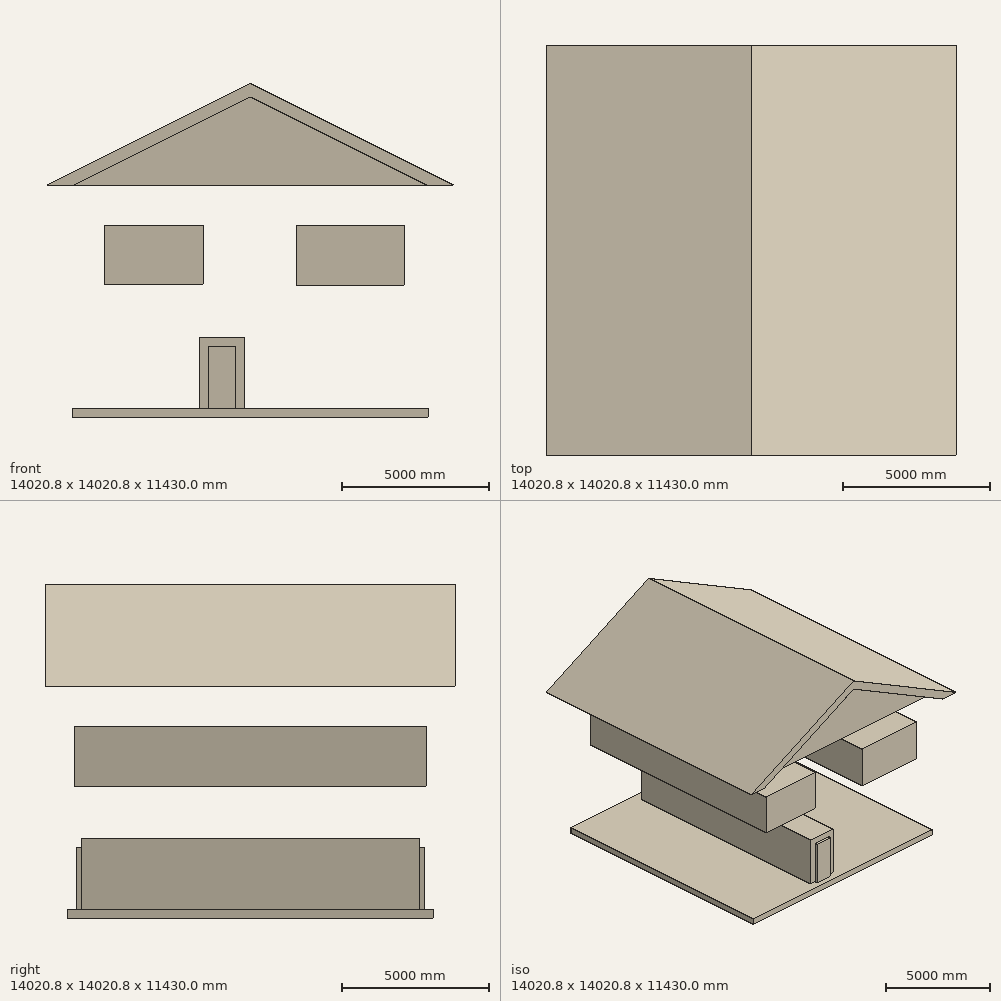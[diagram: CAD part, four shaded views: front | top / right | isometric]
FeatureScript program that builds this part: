
annotation { "Feature Type Name" : "Feature", "Feature Type Description" : "" }
export const myFeature = defineFeature(function(context is Context, id is Id, definition is map)
    precondition{}
    {
        {
            var Q0;
            Q0=qCreatedBy(makeId("Front.planeOp"),FACE);
            var sketch = newSketch(context, id + "F0", { "sketchPlane" : qUnion([Q0])});
            skLineSegment(sketch, "E0", {"start": v(0, 0) * mm, "end": v(-6096, 0) * mm});
            skLineSegment(sketch, "E1", {"start": v(0, 0) * mm, "end": v(6096, 0) * mm});
            skLineSegment(sketch, "E2", {"start": v(0, 0) * mm, "end": v(0, 3048) * mm, "construction": true});
            skLineSegment(sketch, "E3", {"start": v(-6096, 0) * mm, "end": v(0, 3048) * mm});
            skLineSegment(sketch, "E4", {"start": v(0, 3048) * mm, "end": v(6096, 0) * mm});
            skLineSegment(sketch, "E5", {"start": v(0, 3048) * mm, "end": v(0, 3505.2) * mm});
            skLineSegment(sketch, "E6", {"start": v(6096, 0) * mm, "end": v(7010.4, 0) * mm});
            skLineSegment(sketch, "E7", {"start": v(-6096, 0) * mm, "end": v(-7010.4, 0) * mm});
            skLineSegment(sketch, "E8", {"start": v(-7010.4, 0) * mm, "end": v(0, 3505.2) * mm});
            skLineSegment(sketch, "E9", {"start": v(7010.4, 0) * mm, "end": v(0, 3505.2) * mm});
            skLineSegment(sketch, "E10", {"start": v(-6096, 0) * mm, "end": v(-6096, -7620) * mm});
            skLineSegment(sketch, "E11", {"start": v(-6096, -7620) * mm, "end": v(6096, -7620) * mm});
            skLineSegment(sketch, "E12", {"start": v(6096, 0) * mm, "end": v(6096, -7315.2) * mm});
            skLineSegment(sketch, "E13", {"start": v(-6096, -7620) * mm, "end": v(-6096, -7924.8) * mm});
            skLineSegment(sketch, "E14", {"start": v(-6096, -7924.8) * mm, "end": v(6103.47, -7924.8) * mm});
            skLineSegment(sketch, "E15", {"start": v(6103.47, -7924.8) * mm, "end": v(6096, -7620) * mm});
            skLineSegment(sketch, "E16", {"start": v(-1432.56, -7620) * mm, "end": v(-1432.56, -5486.4) * mm});
            skLineSegment(sketch, "E17", {"start": v(-1432.56, -5486.4) * mm, "end": v(-518.16, -5486.4) * mm});
            skLineSegment(sketch, "E18", {"start": v(-518.16, -5486.4) * mm, "end": v(-518.16, -7620) * mm});
            skLineSegment(sketch, "E19.bottom", {"start": v(1560.33, -1350.55) * mm, "end": v(5281.06, -1350.55) * mm});
            skLineSegment(sketch, "E19.top", {"start": v(1560.33, -3402.59) * mm, "end": v(5281.06, -3402.59) * mm});
            skLineSegment(sketch, "E19.left", {"start": v(1560.33, -1350.55) * mm, "end": v(1560.33, -3402.59) * mm});
            skLineSegment(sketch, "E19.right", {"start": v(5281.06, -1350.55) * mm, "end": v(5281.06, -3402.59) * mm});
            skLineSegment(sketch, "E20.bottom", {"start": v(-5001.7, -1350.55) * mm, "end": v(-1619.33, -1350.55) * mm});
            skLineSegment(sketch, "E20.top", {"start": v(-5001.7, -3357.49) * mm, "end": v(-1619.33, -3357.49) * mm});
            skLineSegment(sketch, "E20.left", {"start": v(-5001.7, -1350.55) * mm, "end": v(-5001.7, -3357.49) * mm});
            skLineSegment(sketch, "E20.right", {"start": v(-1619.33, -1350.55) * mm, "end": v(-1619.33, -3357.49) * mm});
            skLineSegment(sketch, "E21.bottom", {"start": v(-941.03, 2243.3) * mm, "end": v(887.77, 2243.3) * mm});
            skLineSegment(sketch, "E21.top", {"start": v(-941.03, 719.3) * mm, "end": v(887.77, 719.3) * mm});
            skLineSegment(sketch, "E21.left", {"start": v(-941.03, 2243.3) * mm, "end": v(-941.03, 719.3) * mm});
            skLineSegment(sketch, "E21.right", {"start": v(887.77, 2243.3) * mm, "end": v(887.77, 719.3) * mm});
            skLineSegment(sketch, "E22.0", {"start": v(-213.36, -5181.6) * mm, "end": v(-213.36, -7620) * mm});
            skLineSegment(sketch, "E22.1", {"start": v(-1737.36, -5181.6) * mm, "end": v(-213.36, -5181.6) * mm});
            skLineSegment(sketch, "E22.2", {"start": v(-1737.36, -7620) * mm, "end": v(-1737.36, -5181.6) * mm});
            skSolve(sketch);
        }
        {
            var Q0;
            Q0=makeQuery(id+"F0.imprint","IMPRINT",FACE,{"disambiguationData":[TD([[makeQuery(id+"F0.imprint","IMPRINT",EDGE,{"derivedFrom":sQuery(id+"F0.wireOp",EDGE,"E3")}),1.0]])]});
            var Q1;
            Q1=makeQuery(id+"F0.imprint","IMPRINT",FACE,{"disambiguationData":[TD([[makeQuery(id+"F0.imprint","IMPRINT",EDGE,{"derivedFrom":sQuery(id+"F0.wireOp",EDGE,"E4")}),1.0]])]});
            extrude(context, id + "F1", {"entities" : qUnion([Q0, Q1]), "endBound" : BoundingType.SYMMETRIC, "depth" : 14020.8 * mm, "offsetDistance" : 30.48 * mm});
        }
        {
            var Q0;
            Q0=makeQuery(id+"F0.imprint","IMPRINT",FACE,{"disambiguationData":[TD([[makeQuery(id+"F0.imprint","IMPRINT",EDGE,{"derivedFrom":sQuery(id+"F0.wireOp",EDGE,"E0")}),-1.0]])]});
            extrude(context, id + "F2", {"entities" : qUnion([Q0]), "operationType" : NewBodyOperationType.ADD, "endBound" : BoundingType.SYMMETRIC, "depth" : 12496.8 * mm, "offsetDistance" : 30.48 * mm});
        }
        {
            var Q0;
            Q0=makeQuery(id+"F0.imprint","IMPRINT",FACE,{"disambiguationData":[TD([[makeQuery(id+"F0.imprint","IMPRINT",EDGE,{"derivedFrom":sQuery(id+"F0.wireOp",EDGE,"E21.bottom")}),-1.0]])]});
            extrude(context, id + "F3", {"entities" : qUnion([Q0]), "operationType" : NewBodyOperationType.ADD, "endBound" : BoundingType.SYMMETRIC, "depth" : 12496.8 * mm, "offsetDistance" : 30.48 * mm});
        }
        {
            var Q0;
            {var subQ5=sQuery(id+"F0.wireOp",EDGE,"E13");Q0=makeQuery(id+"F0.imprint","IMPRINT",FACE,{"disambiguationData":[TD([[makeQuery(id+"F0.imprint","IMPRINT",EDGE,{"derivedFrom":subQ5}),1.0]])]});}
            extrude(context, id + "F4", {"entities" : qUnion([Q0]), "endBound" : BoundingType.SYMMETRIC, "depth" : 12496.8 * mm, "offsetDistance" : 30.48 * mm});
        }
        {
            var Q0;
            Q0=sQuery(id+"F0.wireOp",EDGE,"E10");
            var Q1;
            Q1=sQuery(id+"F0.wireOp",EDGE,"E12");
            extrude(context, id + "F5", {"bodyType" : ToolBodyType.SURFACE, "surfaceEntities" : qUnion([Q0, Q1]), "endBound" : BoundingType.SYMMETRIC, "depth" : 12496.8 * mm, "offsetDistance" : 30.48 * mm});
        }
        {
            var Q0;
            Q0=makeQuery(id+"F0.imprint","IMPRINT",FACE,{"disambiguationData":[TD([[makeQuery(id+"F0.imprint","IMPRINT",EDGE,{"derivedFrom":sQuery(id+"F0.wireOp",EDGE,"E20.bottom")}),-1.0]])]});
            extrude(context, id + "F6", {"entities" : qUnion([Q0]), "endBound" : BoundingType.SYMMETRIC, "depth" : 12039.6 * mm, "offsetDistance" : 30.48 * mm});
        }
        {
            var Q0;
            Q0=makeQuery(id+"F0.imprint","IMPRINT",FACE,{"disambiguationData":[TD([[makeQuery(id+"F0.imprint","IMPRINT",EDGE,{"derivedFrom":sQuery(id+"F0.wireOp",EDGE,"E19.bottom")}),-1.0]])]});
            extrude(context, id + "F7", {"entities" : qUnion([Q0]), "endBound" : BoundingType.SYMMETRIC, "depth" : 12039.6 * mm, "offsetDistance" : 30.48 * mm});
        }
        {
            var Q0;
            {var subQ0=sQuery(id+"F0.wireOp",EDGE,"E16");Q0=makeQuery(id+"F0.imprint","IMPRINT",FACE,{"disambiguationData":[TD([[makeQuery(id+"F0.imprint","IMPRINT",EDGE,{"derivedFrom":subQ0}),-1.0]])]});}
            extrude(context, id + "F8", {"entities" : qUnion([Q0]), "operationType" : NewBodyOperationType.ADD, "endBound" : BoundingType.SYMMETRIC, "depth" : 11887.2 * mm, "offsetDistance" : 30.48 * mm});
        }
        {
            var Q0;
            {var subQ0=sQuery(id+"F0.wireOp",EDGE,"E16");Q0=makeQuery(id+"F0.imprint","IMPRINT",FACE,{"disambiguationData":[TD([[makeQuery(id+"F0.imprint","IMPRINT",EDGE,{"derivedFrom":subQ0}),1.0]])]});}
            extrude(context, id + "F9", {"entities" : qUnion([Q0]), "operationType" : NewBodyOperationType.ADD, "endBound" : BoundingType.SYMMETRIC, "depth" : 11582.4 * mm, "offsetDistance" : 30.48 * mm});
        }
    });
